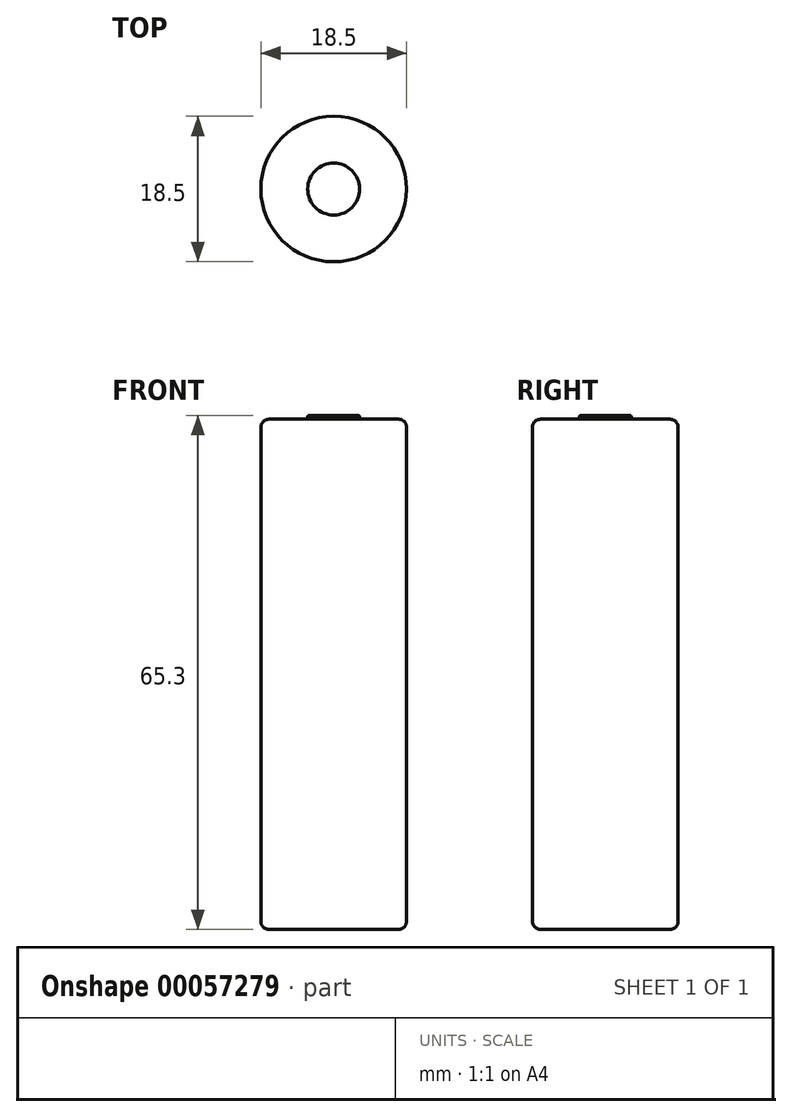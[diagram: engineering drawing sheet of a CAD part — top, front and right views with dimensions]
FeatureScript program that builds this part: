
annotation { "Feature Type Name" : "Feature", "Feature Type Description" : "" }
export const myFeature = defineFeature(function(context is Context, id is Id, definition is map)
    precondition{}
    {
        {
            var Q0;
            Q0=qCreatedBy(makeId("Top.planeOp"),FACE);
            var sketch = newSketch(context, id + "F0", { "sketchPlane" : qUnion([Q0])});
            skCircle(sketch, "E0", {"center": v(0, 0) * mm, "radius": 9.25 * mm});
            skSolve(sketch);
        }
        {
            var Q0;
            Q0=makeQuery(id+"F0.imprint","IMPRINT",FACE,{"disambiguationData":[TD([[makeQuery(id+"F0.imprint","IMPRINT",EDGE,{"derivedFrom":sQuery(id+"F0.wireOp",EDGE,"E0")}),1.0]])]});
            extrude(context, id + "F1", {"entities" : qUnion([Q0]), "depth" : 64.8 * mm});
        }
        {
            var Q0;
            Q0=makeQuery(id+"F1.opExtrude","CAP_FACE",FACE,{"disambiguationData":[OSD([sQuery(id+"F0.wireOp",EDGE,"E0")])],"isStart":false});
            var sketch = newSketch(context, id + "F2", { "sketchPlane" : qUnion([Q0])});
            skCircle(sketch, "E1", {"center": v(0, 0) * mm, "radius": 3.3 * mm});
            skSolve(sketch);
        }
        {
            var Q0;
            Q0 = qSketchRegion(id + "F2", true);
            extrude(context, id + "F3", {"entities" : qUnion([Q0]), "operationType" : NewBodyOperationType.ADD, "depth" : .5 * mm});
        }
        {
            var Q0;
            Q0=makeQuery(id+"F3.opExtrude","CAP_EDGE",EDGE,{"disambiguationData":[OSD([sQuery(id+"F2.wireOp",EDGE,"E1")])],"isStart":false});
            fillet(context, id + "F4", {"entities" : qUnion([Q0]), "radius" : .2 * mm, "tangentPropagation" : true, "allowEdgeOverflow" : false});
        }
        {
            var Q0;
            Q0=makeQuery(id+"F1.opExtrude","CAP_EDGE",EDGE,{"disambiguationData":[OSD([sQuery(id+"F0.wireOp",EDGE,"E0")])],"isStart":false});
            fillet(context, id + "F5", {"entities" : qUnion([Q0]), "radius" : 1 * mm, "tangentPropagation" : true, "allowEdgeOverflow" : false});
        }
        {
            var Q0;
            Q0=makeQuery(id+"F1.opExtrude","CAP_EDGE",EDGE,{"disambiguationData":[OSD([sQuery(id+"F0.wireOp",EDGE,"E0")])],"isStart":true});
            fillet(context, id + "F6", {"entities" : qUnion([Q0]), "radius" : 1 * mm, "tangentPropagation" : true, "allowEdgeOverflow" : false});
        }
    });
